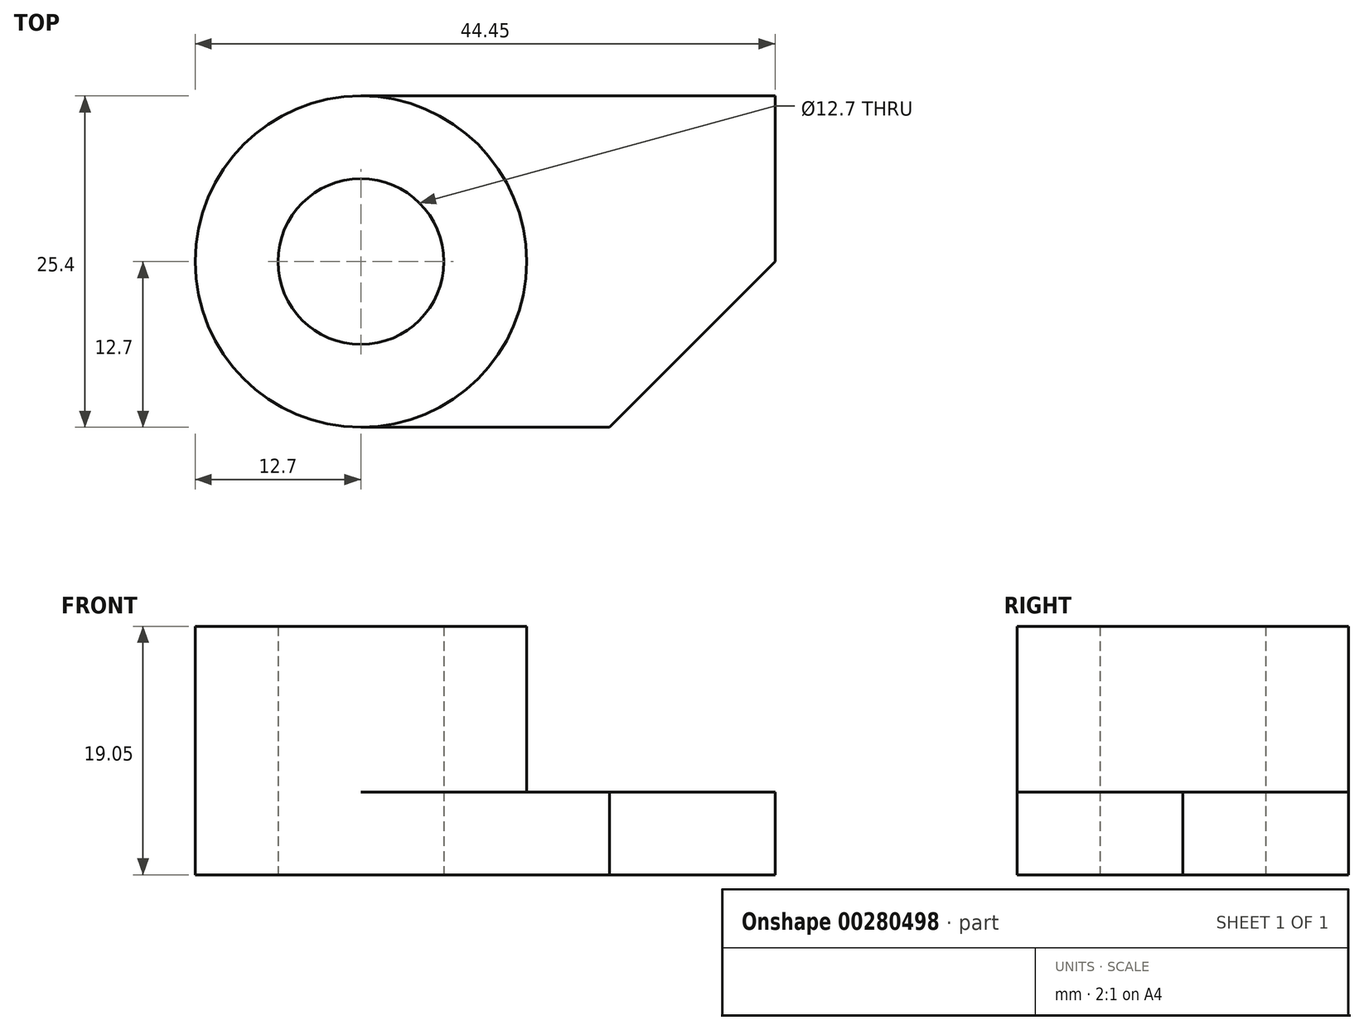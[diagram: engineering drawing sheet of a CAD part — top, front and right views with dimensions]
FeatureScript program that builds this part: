
annotation { "Feature Type Name" : "Feature", "Feature Type Description" : "" }
export const myFeature = defineFeature(function(context is Context, id is Id, definition is map)
    precondition{}
    {
        {
            var Q0;
            Q0=qCreatedBy(makeId("Top.planeOp"),FACE);
            var sketch = newSketch(context, id + "F0", { "sketchPlane" : qUnion([Q0])});
            skCircle(sketch, "E0", {"center": v(0, 0) * mm, "radius": 6.35 * mm});
            skCircle(sketch, "E1", {"center": v(0, 0) * mm, "radius": 12.7 * mm});
            skLineSegment(sketch, "E2", {"start": v(0, -12.7) * mm, "end": v(19.05, -12.7) * mm});
            skLineSegment(sketch, "E3", {"start": v(19.05, -12.7) * mm, "end": v(31.75, -12.7) * mm});
            skLineSegment(sketch, "E4", {"start": v(31.75, -12.7) * mm, "end": v(31.75, 0) * mm});
            skLineSegment(sketch, "E5", {"start": v(31.75, 0) * mm, "end": v(31.75, 12.7) * mm});
            skLineSegment(sketch, "E6", {"start": v(31.75, 12.7) * mm, "end": v(0, 12.7) * mm});
            skLineSegment(sketch, "E7", {"start": v(19.05, -12.7) * mm, "end": v(31.75, 0) * mm});
            skSolve(sketch);
        }
        {
            var Q0;
            Q0=makeQuery(id+"F0.imprint","IMPRINT",FACE,{"disambiguationData":[TD([[makeQuery(id+"F0.imprint","IMPRINT",EDGE,{"derivedFrom":sQuery(id+"F0.wireOp",EDGE,"E0")}),-1.0]])]});
            extrude(context, id + "F1", {"entities" : qUnion([Q0]), "depth" : 19.05 * mm});
        }
        {
            var Q0;
            {var subQ1=sQuery(id+"F0.wireOp",EDGE,"E2");Q0=makeQuery(id+"F0.imprint","IMPRINT",FACE,{"disambiguationData":[TD([[makeQuery(id+"F0.imprint","IMPRINT",EDGE,{"derivedFrom":subQ1}),1.0]])]});}
            extrude(context, id + "F2", {"entities" : qUnion([Q0]), "operationType" : NewBodyOperationType.ADD, "depth" : 6.35 * mm});
        }
    });
